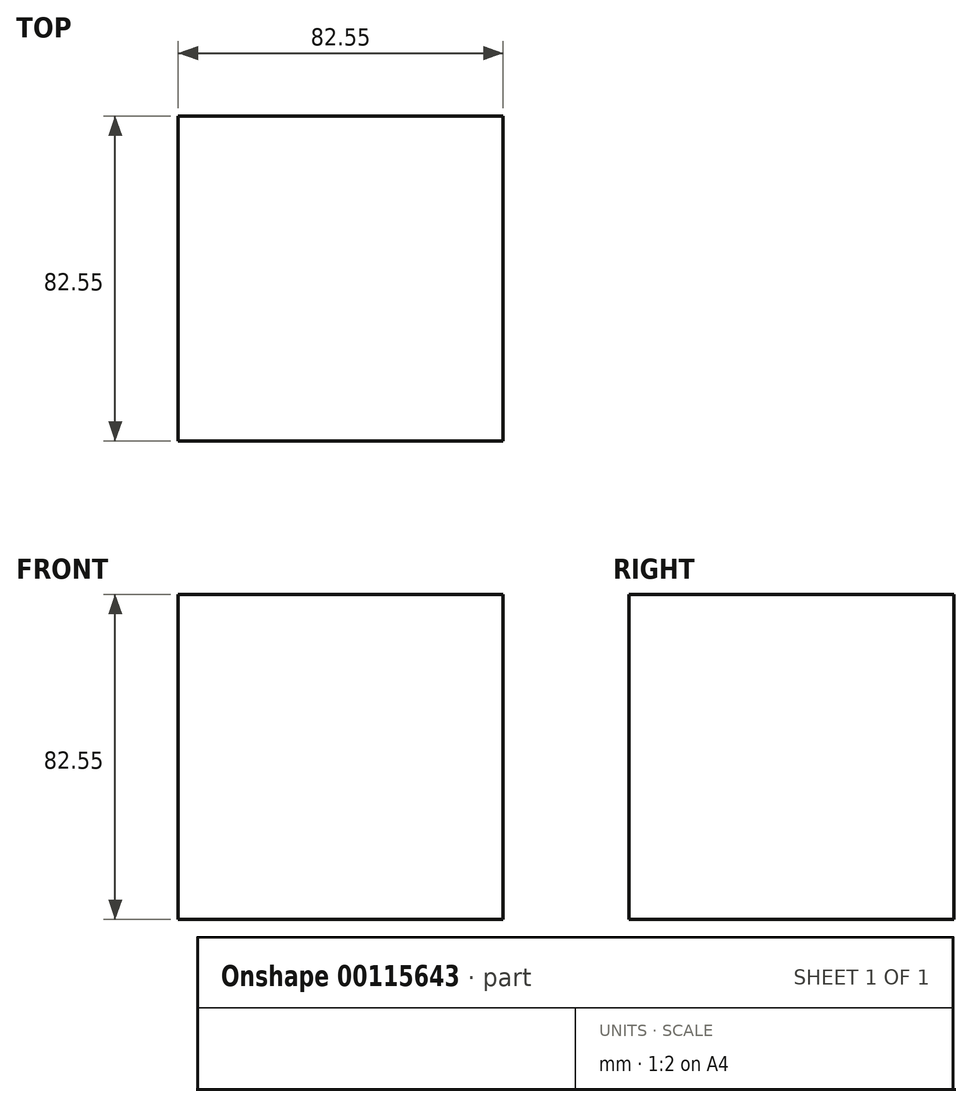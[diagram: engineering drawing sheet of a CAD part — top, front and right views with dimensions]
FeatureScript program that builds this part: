
annotation { "Feature Type Name" : "Feature", "Feature Type Description" : "" }
export const myFeature = defineFeature(function(context is Context, id is Id, definition is map)
    precondition{}
    {
        {
            var Q0;
            Q0=qCreatedBy(makeId("Front.planeOp"),FACE);
            var sketch = newSketch(context, id + "F0", { "sketchPlane" : qUnion([Q0])});
            skLineSegment(sketch, "E0", {"start": v(-36.43, 52.25) * mm, "end": v(46.12, 52.25) * mm});
            skLineSegment(sketch, "E1", {"start": v(-36.43, 52.25) * mm, "end": v(-36.43, -30.3) * mm});
            skLineSegment(sketch, "E2", {"start": v(-36.43, -30.3) * mm, "end": v(46.12, -30.3) * mm});
            skLineSegment(sketch, "E3", {"start": v(46.12, -30.3) * mm, "end": v(46.12, 52.25) * mm});
            skSolve(sketch);
        }
        {
            var Q0;
            Q0=makeQuery(id+"F0.imprint","IMPRINT",FACE,{"disambiguationData":[TD([[makeQuery(id+"F0.imprint","IMPRINT",EDGE,{"derivedFrom":sQuery(id+"F0.wireOp",EDGE,"E0")}),-1.0]])]});
            extrude(context, id + "F1", {"entities" : qUnion([Q0]), "depth" : 82.55 * mm});
        }
        {
            var Q0;
            Q0=makeQuery(id+"F1.opExtrude","CAP_FACE",FACE,{"disambiguationData":[OSD([sQuery(id+"F0.wireOp",EDGE,"E0"),sQuery(id+"F0.wireOp",EDGE,"E1"),sQuery(id+"F0.wireOp",EDGE,"E2"),sQuery(id+"F0.wireOp",EDGE,"E3")])],"isStart":false});
            var sketch = newSketch(context, id + "F2", { "sketchPlane" : qUnion([Q0])});
            skCircle(sketch, "E4", {"center": v(3.24, 11.27) * mm, "radius": 19.09 * mm});
            skSolve(sketch);
        }
        {
            var Q0;
            Q0 = qSketchRegion(id + "F2", true);
            extrude(context, id + "F3", {"entities" : qUnion([Q0]), "operationType" : NewBodyOperationType.REMOVE, "oppositeDirection" : true, "depth" : 25.4 * mm});
        }
        {
            var Q0;
            Q0=makeQuery(id+"F3.boolean.opBoolean","COPY",FACE,{"derivedFrom":makeQuery(id+"F3.opExtrude","CAP_FACE",FACE,{"disambiguationData":[OSD([sQuery(id+"F2.wireOp",EDGE,"E4")])],"isStart":false})});
            extrude(context, id + "F4", {"entities" : qUnion([Q0]), "operationType" : NewBodyOperationType.ADD, "depth" : 25.4 * mm});
        }
    });
